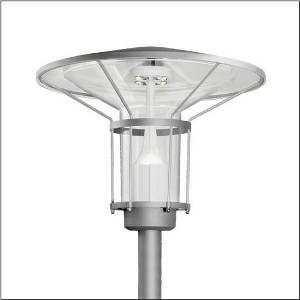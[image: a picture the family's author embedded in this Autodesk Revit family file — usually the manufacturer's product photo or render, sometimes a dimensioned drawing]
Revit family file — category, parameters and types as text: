
# Revit family: laterne_classic___p1_0a_5xa5245ff14h_055f
name_source: partatom
category: Lighting Fixtures
units: mm (PartAtom-declared; Revit-internal decimal feet)

## family parameters
Cut with Voids When Loaded = No
Host = Face
Light Source = No
Part Type = Normal
Room Calculation Point = No
Round Connector Dimension = Use Diameter
Shared = No

## types (1)
- --- (1 x LED, 1360 lm, 10.5 W, 3000K)
    Apparent Load = 11 VA
    CIE Flux Codes = 30 61 91 96 100
    Color Rendering = 70
    Color Temperature = 3000K
    Default Elevation = 1800 mm
    Description = Lantern Classic, mast luminaire, Module 540 iQ-SR, primary light control with 3 zone facetted reflector, of plastic, silver coated, highly specular, structured, primary optical cover: cover, of PMMA, transparent, light distribution: P1.0a, light emission: direct distribution, primary light characteristic: strongly asymmetric, installation type: post-top, LED, High Power LED, rated luminous flux: 1.360lm, luminous efficacy: 130lm/W, light colour: 730, colour temperature: 3000K, control gear: ECG iQ, control: Auto-Match, Temp-Guard, Lumen-Switch, Night-Set, Smart-Wire, Light-Fading, Desk-Remote (wireless, voltage-free reading and setting of iQ features in the workshop via application-optimized NFC function/RFID function), optimised constant luminous flux control (CLO 2.0), Street-Remote, presetting dimming logarithmic, with terminal, 6-pole, max. 2.5mm², mains connection: 220..240V, AC, 50/60Hz, start of lifetime: 11W, end of lifetime: 11W, reduction: 5W, luminaire housing, upper part, of glass-fibre reinforced polyester, coated, Siteco® metallic grey (DB 702S), diameter: 750mm, height: 596mm, spigot size: d x l = 76 x 70mm (post-top) | with reducer (optional accessory) 60 x 70mm, post-top mast mounting element, of diecast aluminium, coated, Siteco® metallic grey (DB 702S), Module 540 iQ-SR, traffic white (RAL 9016), equipment: standard, protection rating (complete): IP65, insulation class (complete): insulation class II (safety insulation), certification: CE, ENEC, VDE, packaging unit: 1 piece

Light Distribution: P1.0a
    Height = 596 mm
    Lamp = 1 x LED
    Lamp Light Flux = 1360 lm
    Lamp Power = 10.5 W
    Lamp count = 1
    Length = 750 mm
    Luminous efficacy = 130 lm/W
    Manufacturer = Siteco
    ModVariant = No
    Model = 5XA5245FF14H
    Number of Poles = 1
    OnlyDefault = Yes
    Power Factor = 1
    Product Name = Laterne Classic | P1.0a
    Product group = mast luminaire | pylon top
    ProductGroupID = 6100
    Protection Class = Protection class II
    Protection Degree = IP 65
    RLX_Detail_Level = 1
    RlxData = <blob elided: 94333 chars, md5=3a475db4>
    Socket = socket
    Standby Power = 0 W
    System Light Flux = 1360 lm
    System Power = 11 W
    Type Comments = factory setting: luminous flux: 100 % | dim-lin: 254 | 419 mA
    Type Image = l_1006052.jpg
    URL = http://relux.com
    VarID = @adj_071491
    Voltage = 0 V
    Weight = 0.00 kg
    Width = 0 mm  [stored 0 ft]

note: [stored X ft] marks values corroborated as IEEE doubles in the binary element streams (Revit-internal decimal feet)

## geometry (parser evidence)
native form markers: Blend x4, Sweep x12
no freeform markers — native parametric forms only
